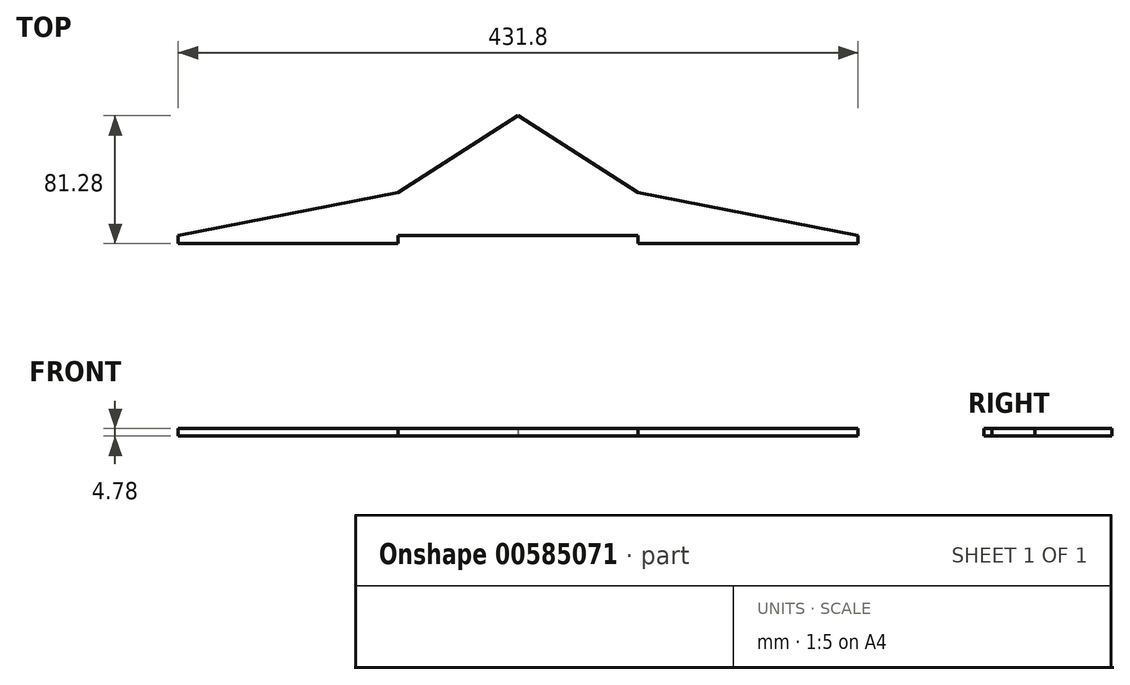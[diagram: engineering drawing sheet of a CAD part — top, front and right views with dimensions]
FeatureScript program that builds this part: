
annotation { "Feature Type Name" : "Feature", "Feature Type Description" : "" }
export const myFeature = defineFeature(function(context is Context, id is Id, definition is map)
    precondition{}
    {
        {
            var Q0;
            Q0=qCreatedBy(makeId("Top.planeOp"),FACE);
            var sketch = newSketch(context, id + "F0", { "sketchPlane" : qUnion([Q0])});
            skLineSegment(sketch, "E0.top", {"start": v(186.3, 28.82) * mm, "end": v(46.6, 28.82) * mm});
            skLineSegment(sketch, "E1.bottom", {"start": v(46.6, 28.82) * mm, "end": v(186.3, 28.82) * mm});
            skLineSegment(sketch, "E2", {"start": v(46.6, 33.9) * mm, "end": v(46.6, 28.82) * mm});
            skLineSegment(sketch, "E3", {"start": v(186.3, 28.82) * mm, "end": v(186.3, 33.9) * mm});
            skLineSegment(sketch, "E4", {"start": v(46.6, 61.26) * mm, "end": v(186.3, 33.9) * mm});
            skLineSegment(sketch, "E5", {"start": v(-29.6, 110.1) * mm, "end": v(-29.6, 33.9) * mm});
            skLineSegment(sketch, "E6", {"start": v(46.6, 33.9) * mm, "end": v(-29.6, 33.9) * mm});
            skLineSegment(sketch, "E7.MirrorCS", {"start": v(-245.5, 28.82) * mm, "end": v(-245.5, 33.9) * mm});
            skLineSegment(sketch, "E8.MirrorCS", {"start": v(-105.8, 33.9) * mm, "end": v(-105.8, 28.82) * mm});
            skLineSegment(sketch, "E9.MirrorCS", {"start": v(-245.5, 28.82) * mm, "end": v(-105.8, 28.82) * mm});
            skLineSegment(sketch, "E10.MirrorCS", {"start": v(-105.8, 61.26) * mm, "end": v(-245.5, 33.9) * mm});
            skLineSegment(sketch, "E11.MirrorCS", {"start": v(-105.8, 28.82) * mm, "end": v(-245.5, 28.82) * mm});
            skLineSegment(sketch, "E12.MirrorCS", {"start": v(-105.8, 33.9) * mm, "end": v(-29.6, 33.9) * mm});
            skLineSegment(sketch, "E13", {"start": v(-105.8, 61.26) * mm, "end": v(-29.6, 110.1) * mm});
            skLineSegment(sketch, "E14", {"start": v(-29.6, 110.1) * mm, "end": v(46.6, 61.26) * mm});
            skSolve(sketch);
        }
        {
            var Q0;
            Q0 = qSketchRegion(id + "F0", true);
            extrude(context, id + "F1", {"entities" : qUnion([Q0]), "depth" : 4.78 * mm, "offsetDistance" : 25.4 * mm});
        }
    });
